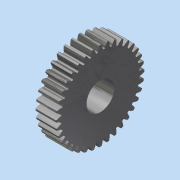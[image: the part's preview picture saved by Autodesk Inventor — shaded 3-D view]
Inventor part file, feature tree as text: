
AUTODESK INVENTOR PART (.ipt)
format: ipt  version: 2015 (Build 190159000, 159)  size: 1,482,240 bytes
history: native  units: in
note: dims shown in document units (in); Inventor stores cm internally (conversion verified against a paired STEP export)
features: other x1, plane x1, split x1, imported_body x1
ambient origin geometry x8: Origin, YZ Plane, XZ Plane, XY Plane, X Axis, Y Axis, Z Axis, Center Point
bodies: Solid1 (feature_tree)
feature tree (4):
  other  "s1086z-048s0361"
  plane  "Work Plane1"
  split  "Split1"
  imported_body  "Base1"
